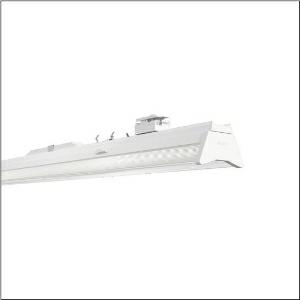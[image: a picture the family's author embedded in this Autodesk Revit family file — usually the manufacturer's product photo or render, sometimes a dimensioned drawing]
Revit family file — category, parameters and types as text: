
# Revit family: licross_11_performance_mo_51tm16dn445g
name_source: partatom
category: Lighting Fixtures
units: mm (PartAtom-declared; Revit-internal decimal feet)

## family parameters
Cut with Voids When Loaded = No
Host = Face
Light Source = No
Part Type = Normal
Room Calculation Point = No
Round Connector Dimension = Use Diameter
Shared = No

## types (1)
- --- (1 x LED, 4520 lm, 24.3 W, 4000K)
    Apparent Load = 24 VA
    CIE Flux Codes = 66 88 96 79 100
    Color Rendering = 80
    Color Temperature = 4000K
    Default Elevation = 1800 mm
    Description = Licross 11 Performance MO, luminaire insert, of sheet steel, galvanised, coil coated, white, length: 1.500mm, width: 120mm, height: 123mm, LED rated luminous flux: 4.520lm, light colour: 840, SDCM (Standard Deviation of Colour Matching)MacAdam ≤ 2 SDCM (initial), control gear: DALI 2, with plug, 5-pole, with phase selection, mains connection: 220..240V, AC, 50/60Hz, rated input power: 24W, internal wiring halogen-free, primary light control with lens, of plastic, primary optical cover: cover, of PMMA, CAT 2 (L<= 3000cd/m²), light emission: direct/indirect distribution, primary light characteristic: symmetric, protection rating (complete): IP40, insulation class (complete): insulation class I (protective earthing), certification: CE, ENEC, VDE, UKCA, protection symbol: D if used in an environment without relevant dust loads with corresponding accessories, impact resistance: IK06, permissible ambient temperature for indoor applications: -25..+45°C, corresponds to IFS (International Featured Standards) requirements for safety and quality in the food industry, reducing of maximum allowable ambient temperature of 5°C with ceiling mounting, LABS conformity tested according to VDMA 24364:2018-05, The light source and the operating device comply with the requirements of the Ecodesign Regulation (EU) 2019/2020 and are replaceable in accordance with this regulation, packaging unit: 1 piece
    Height = 114 mm
    Lamp = 1 x LED
    Lamp Light Flux = 4520 lm
    Lamp Power = 24.3 W
    Lamp count = 1
    Length = 1500 mm
    Luminous efficacy = 186 lm/W
    Manufacturer = Siteco
    ModVariant = No
    Model = 51TM16DN445G
    Mounting Place = Ceiling
    Mounting Type = Pendant
    Number of Poles = 1
    OnlyDefault = Yes
    Power Factor = 1
    Product Name = Licross 11 Performance MO
    Product group = luminaire insert | ceiling pendant
    ProductGroupID = 901
    Protection Class = Protection class I
    Protection Degree = IP 40
    RLX_Detail_Level = 1
    RLX_Emergency_Light_Flux = 0 lm
    RLX_Emergency_Type = 0
    RLX_Emergency_Type_DB = No
    RlxData = <blob elided: 34041 chars, md5=ebde88d1>
    Socket = socket
    Standby Power = 0 W
    System Light Flux = 4520 lm
    System Power = 24 W
    Type Comments = factory setting: luminous flux: 100 % | dim-lin: 254 | 161 mA
    Type Image = l_1256138.jpg
    URL = http://relux.com
    VarID = @adj_056321
    Voltage = 0 V
    Weight = 0.00 kg
    Width = 120 mm

## geometry (parser evidence)
native form markers: Blend x4, Sweep x11
no freeform markers — native parametric forms only
